FCSTD DOCUMENT  (FreeCAD 0.21R33668 +26 (Git))
Label: plan cuisine
License: All rights reserved
LicenseURL: http://en.wikipedia.org/wiki/All_rights_reserved
objects: App::FeaturePython×10, PartDesign::Body×1, Sketcher::SketchObject×1, App::DocumentObjectGroup×1, Part::Part2DObjectPython×1
note: 3 computed .brp shape members not serialized (recipe doc carries the construction recipe); baked Part::Feature solids carry a one-line shape summary decoded from their .brp

FEATURE [PartDesign::Body] Body
  Origin = -> Origin
FEATURE [Sketcher::SketchObject] Sketch
  FullyConstrained = false
  MapMode = 5
  Support = -> [XY_Plane]
  sketch-geometry (25):
    g0: LineSegment StartX=-2200 StartY=2044.26 StartZ=0 EndX=2200 EndY=2044.26 EndZ=0
    g1: LineSegment StartX=2200 StartY=2044.26 StartZ=0 EndX=2200 EndY=474.259 EndZ=0
    g2: LineSegment StartX=2200 StartY=474.259 StartZ=0 EndX=2000 EndY=474.259 EndZ=0
    g3: LineSegment StartX=2000 StartY=474.259 StartZ=0 EndX=2000 EndY=1844.26 EndZ=0
    g4: LineSegment StartX=2000 StartY=1844.26 StartZ=0 EndX=-2000 EndY=1844.26 EndZ=0
    g5: LineSegment StartX=-2000 StartY=1844.26 StartZ=0 EndX=-2000 EndY=644.259 EndZ=0
    g6: LineSegment StartX=-2000 StartY=644.259 StartZ=0 EndX=-2200 EndY=644.259 EndZ=0
    g7: LineSegment StartX=-2200 StartY=644.259 StartZ=0 EndX=-2200 EndY=2044.26 EndZ=0
    g8: LineSegment StartX=-2200 StartY=-555.741 StartZ=0 EndX=-2200 EndY=-1855.74 EndZ=0
    g9: LineSegment StartX=-2200 StartY=-1855.74 StartZ=0 EndX=2200 EndY=-1855.74 EndZ=0
    g10: LineSegment StartX=2200 StartY=-1855.74 StartZ=0 EndX=2200 EndY=-255.741 EndZ=0
    g11: LineSegment StartX=2200 StartY=-255.741 StartZ=0 EndX=2000 EndY=-255.741 EndZ=0
    g12: LineSegment StartX=2000 StartY=-255.741 StartZ=0 EndX=2000 EndY=-1655.74 EndZ=0
    g13: LineSegment StartX=2000 StartY=-1655.74 StartZ=0 EndX=-2000 EndY=-1655.74 EndZ=0
    g14: LineSegment StartX=-2000 StartY=-1655.74 StartZ=0 EndX=-2000 EndY=-555.741 EndZ=0
    g15: LineSegment StartX=-2000 StartY=-555.741 StartZ=0 EndX=-2200 EndY=-555.741 EndZ=0
    g16: Circle CenterX=0 CenterY=-1567.11 CenterZ=0 NormalX=0 NormalY=0 NormalZ=1 AngleXU=0 Radius=50.3859
    g17: LineSegment StartX=-2725.23 StartY=44.2594 StartZ=0 EndX=-1442.24 EndY=44.2594 EndZ=0
    g18: ArcOfCircle CenterX=-1866.46 CenterY=35.6981 CenterZ=0 NormalX=0 NormalY=0 NormalZ=1 AngleXU=0 Radius=617.356 StartAngle=4.5008 EndAngle=7.92224
    g19: LineSegment StartX=-1866.46 StartY=35.6981 StartZ=0 EndX=-1249.1 EndY=35.6981 EndZ=0
    g20: LineSegment StartX=2218.14 StartY=-177.533 StartZ=0 EndX=2253.9 EndY=-177.533 EndZ=0
    g21: LineSegment StartX=2253.9 StartY=-177.533 StartZ=0 EndX=2253.9 EndY=-996.477 EndZ=0
    g22: LineSegment StartX=2253.9 StartY=-996.477 StartZ=0 EndX=2218.14 EndY=-996.477 EndZ=0
    g23: LineSegment StartX=2218.14 StartY=-996.477 StartZ=0 EndX=2218.14 EndY=-177.533 EndZ=0
    g24: LineSegment StartX=-2100 StartY=644.259 StartZ=0 EndX=-2100 EndY=-555.741 EndZ=0
  constraints (61):
    c: Horizontal(g0)
    c: Coincident(g1,g0)
    c: Vertical(g1)
    c: Coincident(g2,g1)
    c: Horizontal(g2)
    c: Coincident(g3,g2)
    c: Vertical(g3)
    c: Coincident(g4,g3)
    c: Coincident(g5,g4)
    c: Vertical(g5)
    c: Horizontal(g6)
    c: Coincident(g7,g6)
    c: Coincident(g7,g0)
    c: Vertical(g7)
    c: DistanceX(g6,g6) = 200
    c: DistanceX(g2,g2) = 200
    c: DistanceX(g0,g0) = 4400
    c: DistanceY(g4,g0) = 200
    c: DistanceY(g5,g5) = 1200
    c: DistanceY(g3,g3) = 1370
    c: Symmetric(g4,g3,g-2)
    c: Vertical(g8)
    c: Coincident(g9,g8)
    c: Coincident(g10,g9)
    c: Vertical(g10)
    c: Coincident(g11,g10)
    c: Horizontal(g11)
    c: Coincident(g12,g11)
    c: Vertical(g12)
    c: Coincident(g13,g12)
    c: Horizontal(g13)
    c: Coincident(g14,g13)
    c: Vertical(g14)
    c: Coincident(g15,g8)
    c: Equal(g9,g0)
    c: Equal(g15,g6)
    c: Horizontal(g15)
    c: Equal(g11,g2)
    c: DistanceY(g8,g13) = 200
    c: Symmetric(g8,g9,g-2)
    c: DistanceY(g14,g14) = 1100
    c: DistanceY(g12,g12) = 1400
    c: DistanceY(g13,g4) = 3500
    c: PointOnObject(g16,g-2)
    c: Symmetric(g5,g14,g17)
    c: Coincident(g19,g18)
    c: PointOnObject(g19,g18)
    c: Horizontal(g19)
    c: Coincident(g20,g21)
    c: Coincident(g21,g22)
    c: Coincident(g22,g23)
    c: Coincident(g23,g20)
    c: Horizontal(g20)
    c: Horizontal(g22)
    c: Vertical(g21)
    c: Vertical(g23)
    c: Coincident(g15,g14)
    c: Coincident(g6,g5)
    c: PointOnObject(g24,g6)
    c: PointOnObject(g24,g15)
    c: Vertical(g24)
FEATURE [App::FeaturePython] Dimension  # Draft dimension (typed FeaturePython)
  Diameter = false
  Dimline = (-293,2747.46,0)
  Direction = (0,0,0)
  Distance = 4000
  End = (-2000,1844.26,0)
  LinkedGeometry = -> [Sketch]
  Normal = (0,0,1)
  Start = (2000,1844.26,0)
  Support = -> Sketch
FEATURE [App::DocumentObjectGroup] Draft_Construction  label="Construction"
FEATURE [App::FeaturePython] Dimension001  # Draft dimension (typed FeaturePython)
  Diameter = false
  Dimline = (3184,-1381.54,0)
  Direction = (0,0,0)
  Distance = 3500
  End = (2000,-1648.16,0)
  Normal = (0,0,1)
  Start = (2000,1851.84,0)
FEATURE [App::FeaturePython] Dimension002  # Draft dimension (typed FeaturePython)
  Diameter = false
  Dimline = (-3069,1346.46,0)
  Direction = (0,0,0)
  Distance = 1200
  End = (-2000,644.259,0)
  LinkedGeometry = -> [Sketch]
  Normal = (0,0,1)
  Start = (-2000,1844.26,0)
  Support = -> Sketch
FEATURE [App::FeaturePython] Dimension003  # Draft dimension (typed FeaturePython)
  Diameter = false
  Dimline = (-3069,-266.536,0)
  Direction = (0,0,0)
  Distance = 1100
  End = (-2000,-555.741,0)
  LinkedGeometry = -> [Sketch]
  Normal = (0,0,1)
  Start = (-2000,-1655.74,0)
  Support = -> Sketch
FEATURE [App::FeaturePython] Dimension004  # Draft dimension (typed FeaturePython)
  Diameter = false
  Dimline = (2632,1414.46,0)
  Direction = (0,0,0)
  Distance = 1370
  End = (2000,1844.26,0)
  LinkedGeometry = -> [Sketch]
  Normal = (0,0,1)
  Start = (2000,474.259,0)
  Support = -> Sketch
FEATURE [App::FeaturePython] Dimension005  # Draft dimension (typed FeaturePython)
  Diameter = false
  Dimline = (2671,-794.536,0)
  Direction = (0,0,0)
  Distance = 1400
  End = (2000,-1655.74,0)
  LinkedGeometry = -> [Sketch]
  Normal = (0,0,1)
  Start = (2000,-255.741,0)
  Support = -> Sketch
FEATURE [App::FeaturePython] Text  # WARN: FeaturePython — macro-defined, semantics opaque (R4)
  Placement = pos=(-1940,-1597.5,0) rot=(0,0,1;0rad)
  Text = arrivee/evacuation eau
FEATURE [App::FeaturePython] Dimension006  # Draft dimension (typed FeaturePython)
  Diameter = false
  Dimline = (1693,-2408.54,0)
  Direction = (0,0,0)
  Distance = 1984.72
  End = (2000,-1648.16,0)
  Normal = (0,0,1)
  Start = (15.2863,-1644.16,0)
FEATURE [App::FeaturePython] Text001  # WARN: FeaturePython — macro-defined, semantics opaque (R4)
  Placement = pos=(379,-1397.5,0) rot=(0,0,1;0rad)
  Text = Evacuation hote
FEATURE [App::FeaturePython] Text002  # WARN: FeaturePython — macro-defined, semantics opaque (R4)
  Placement = pos=(-5172,2151.46,0) rot=(0,0,1;0rad)
  Text = Machine Vaisselle | Machine Linge | Bouteille gaz | Poubelles
FEATURE [Part::Part2DObjectPython] Line  # Draft 2D object (typed FeaturePython)
  Area = 0
  ChamferSize = 0
  Closed = false
  End = (363,-1392.54,0)
  FilletRadius = 0
  Length = 304.6
  MakeFace = true
  Placement = pos=(93,-1533.54,0) rot=(0,0,1;0rad)
  Points = (2) [(0,0,0),(270,141,0)]
  Start = (93,-1533.54,0)
  Subdivisions = 0
